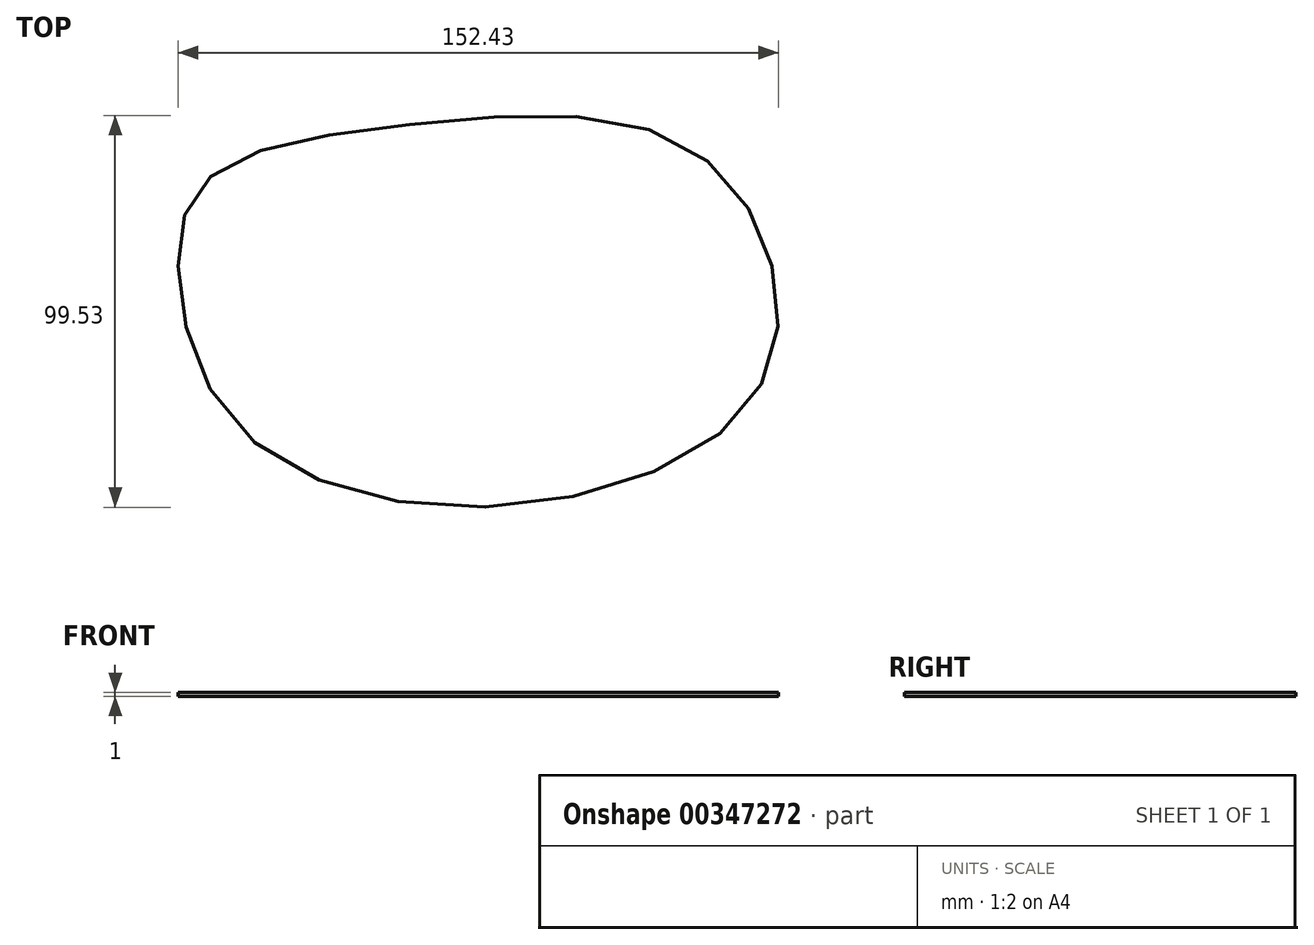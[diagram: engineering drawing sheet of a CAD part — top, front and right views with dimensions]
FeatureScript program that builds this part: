
annotation { "Feature Type Name" : "Feature", "Feature Type Description" : "" }
export const myFeature = defineFeature(function(context is Context, id is Id, definition is map)
    precondition{}
    {
        {
            var Q0;
            Q0=qCreatedBy(makeId("Top.planeOp"),FACE);
            var sketch = newSketch(context, id + "F0", { "sketchPlane" : qUnion([Q0])});
            skFitSpline(sketch, "E0", {"points": [v(-21.77, 35.85) * mm, v(-71.94, 23.03) * mm, v(-80.56, 0) * mm, v(-64.72, -41.67) * mm, v(0, -61.25) * mm, v(63.16, -36.7) * mm, v(70.29, 0) * mm, v(44.82, 32.33) * mm, v(-21.77, 35.85) * mm]});
            skSolve(sketch);
        }
        {
            var Q0;
            Q0 = qSketchRegion(id + "F0", true);
            extrude(context, id + "F1", {"entities" : qUnion([Q0]), "depth" : 1 * mm});
        }
    });
